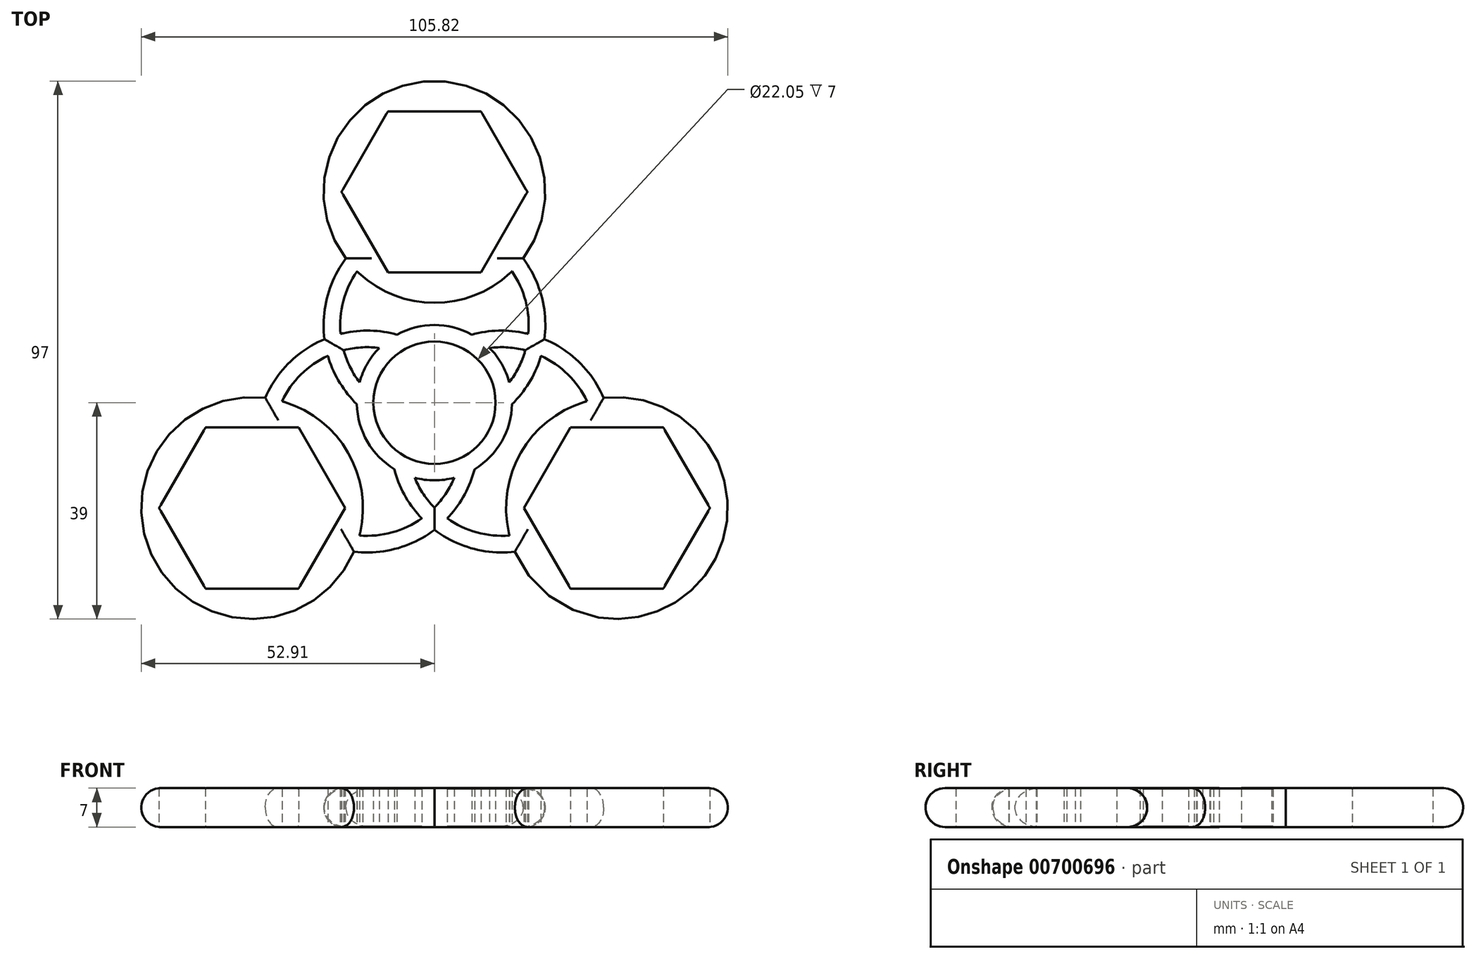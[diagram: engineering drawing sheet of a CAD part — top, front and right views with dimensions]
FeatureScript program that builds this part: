
annotation { "Feature Type Name" : "Feature", "Feature Type Description" : "" }
export const myFeature = defineFeature(function(context is Context, id is Id, definition is map)
    precondition{}
    {
        {
            var Q0;
            Q0=qCreatedBy(makeId("Top.planeOp"),FACE);
            var sketch = newSketch(context, id + "F0", { "sketchPlane" : qUnion([Q0])});
            skCircle(sketch, "E0", {"center": v(0, 0) * mm, "radius": 11.03 * mm});
            skCircle(sketch, "E1", {"center": v(0, 0) * mm, "radius": 14 * mm});
            skCircle(sketch, "E2.cCircle", {"center": v(0, 38) * mm, "radius": 14.52 * mm, "construction": true});
            skLineSegment(sketch, "E2.0", {"start": v(16.77, 38) * mm, "end": v(8.39, 23.48) * mm});
            skLineSegment(sketch, "E2.1", {"start": v(8.39, 23.47) * mm, "end": v(-8.39, 23.47) * mm});
            skLineSegment(sketch, "E2.2", {"start": v(-8.39, 23.48) * mm, "end": v(-16.77, 38) * mm});
            skLineSegment(sketch, "E2.3", {"start": v(-16.77, 38) * mm, "end": v(-8.39, 52.53) * mm});
            skLineSegment(sketch, "E2.4", {"start": v(-8.39, 52.52) * mm, "end": v(8.39, 52.52) * mm});
            skLineSegment(sketch, "E2.5", {"start": v(8.39, 52.52) * mm, "end": v(16.77, 38) * mm});
            skPoint(sketch, "E2.0.midPoint", {"position": v(12.58, 30.74) * mm});
            skCircle(sketch, "E3", {"center": v(0, 38) * mm, "radius": 20 * mm});
            skCircle(sketch, "E4", {"center": v(0, 14) * mm, "radius": 20 * mm});
            skCircle(sketch, "E5", {"center": v(0, 14) * mm, "radius": 17 * mm});
            skSolve(sketch);
        }
        {
            var Q0;
            {var subQ0=sQuery(id+"F0.wireOp",EDGE,"E2.3");Q0=makeQuery(id+"F0.imprint","IMPRINT",FACE,{"disambiguationData":[TD([[makeQuery(id+"F0.imprint","IMPRINT",EDGE,{"derivedFrom":subQ0}),1.0]])]});}
            var Q1;
            {var subQ0=sQuery(id+"F0.wireOp",EDGE,"E5");var subQ1=sQuery(id+"F0.wireOp",EDGE,"E2.1");var subQ2=makeQuery(id+"F0.imprint","INTERSECT",VERTEX,{"disambiguationData":[OD(0.0)],"derivedFrom":[subQ1,subQ0]});Q1=makeQuery(id+"F0.imprint","IMPRINT",FACE,{"disambiguationData":[TD([[makeQuery(id+"F0.imprint","IMPRINT",EDGE,{"disambiguationData":[TD([[subQ2,-1.0]])],"derivedFrom":subQ1}),1.0]])]});}
            var Q2;
            {var subQ3=sQuery(id+"F0.wireOp",EDGE,"E2.2");var subQ5=sQuery(id+"F0.wireOp",EDGE,"E2.1");var subQ6=makeQuery(id+"F0.imprint","INTERSECT",VERTEX,{"derivedFrom":[subQ5,subQ3]});Q2=makeQuery(id+"F0.imprint","IMPRINT",FACE,{"disambiguationData":[TD([[makeQuery(id+"F0.imprint","IMPRINT",EDGE,{"disambiguationData":[TD([[subQ6,1.0]])],"derivedFrom":subQ5}),1.0]])]});}
            var Q3;
            {var subQ3=sQuery(id+"F0.wireOp",EDGE,"E2.0");var subQ7=sQuery(id+"F0.wireOp",EDGE,"E2.1");var subQ8=makeQuery(id+"F0.imprint","INTERSECT",VERTEX,{"derivedFrom":[subQ3,subQ7]});Q3=makeQuery(id+"F0.imprint","IMPRINT",FACE,{"disambiguationData":[TD([[makeQuery(id+"F0.imprint","IMPRINT",EDGE,{"disambiguationData":[TD([[subQ8,1.0]])],"derivedFrom":subQ3}),1.0]])]});}
            var Q4;
            {var subQ0=sQuery(id+"F0.wireOp",EDGE,"E4");var subQ1=sQuery(id+"F0.wireOp",EDGE,"E1");var subQ2=makeQuery(id+"F0.imprint","INTERSECT",VERTEX,{"disambiguationData":[OD(1.0)],"derivedFrom":[subQ1,subQ0]});Q4=makeQuery(id+"F0.imprint","IMPRINT",FACE,{"disambiguationData":[TD([[makeQuery(id+"F0.imprint","IMPRINT",EDGE,{"disambiguationData":[TD([[subQ2,1.0]])],"derivedFrom":subQ1}),-1.0]])]});}
            var Q5;
            {var subQ0=sQuery(id+"F0.wireOp",EDGE,"E4");var subQ1=sQuery(id+"F0.wireOp",EDGE,"E1");var subQ2=makeQuery(id+"F0.imprint","INTERSECT",VERTEX,{"disambiguationData":[OD(0.0)],"derivedFrom":[subQ1,subQ0]});Q5=makeQuery(id+"F0.imprint","IMPRINT",FACE,{"disambiguationData":[TD([[makeQuery(id+"F0.imprint","IMPRINT",EDGE,{"disambiguationData":[TD([[subQ2,-1.0]])],"derivedFrom":subQ1}),-1.0]])]});}
            var Q6;
            {var subQ0=sQuery(id+"F0.wireOp",EDGE,"E5");var subQ1=sQuery(id+"F0.wireOp",EDGE,"E0");var subQ2=makeQuery(id+"F0.imprint","INTERSECT",VERTEX,{"disambiguationData":[OD(0.0)],"derivedFrom":[subQ1,subQ0]});Q6=makeQuery(id+"F0.imprint","IMPRINT",FACE,{"disambiguationData":[TD([[makeQuery(id+"F0.imprint","IMPRINT",EDGE,{"disambiguationData":[TD([[subQ2,1.0]])],"derivedFrom":subQ1}),-1.0]])]});}
            var Q7;
            {var subQ0=sQuery(id+"F0.wireOp",EDGE,"E5");var subQ1=sQuery(id+"F0.wireOp",EDGE,"E0");var subQ2=makeQuery(id+"F0.imprint","INTERSECT",VERTEX,{"disambiguationData":[OD(1.0)],"derivedFrom":[subQ1,subQ0]});Q7=makeQuery(id+"F0.imprint","IMPRINT",FACE,{"disambiguationData":[TD([[makeQuery(id+"F0.imprint","IMPRINT",EDGE,{"disambiguationData":[TD([[subQ2,-1.0]])],"derivedFrom":subQ1}),-1.0]])]});}
            var Q8;
            {var subQ0=sQuery(id+"F0.wireOp",EDGE,"E5");var subQ1=sQuery(id+"F0.wireOp",EDGE,"E0");var subQ2=makeQuery(id+"F0.imprint","INTERSECT",VERTEX,{"disambiguationData":[OD(0.0)],"derivedFrom":[subQ1,subQ0]});Q8=makeQuery(id+"F0.imprint","IMPRINT",FACE,{"disambiguationData":[TD([[makeQuery(id+"F0.imprint","IMPRINT",EDGE,{"disambiguationData":[TD([[subQ2,-1.0]])],"derivedFrom":subQ1}),-1.0]])]});}
            var Q9;
            {var subQ0=sQuery(id+"F0.wireOp",EDGE,"E4");var subQ1=sQuery(id+"F0.wireOp",EDGE,"E0");var subQ2=makeQuery(id+"F0.imprint","INTERSECT",VERTEX,{"disambiguationData":[OD(0.0)],"derivedFrom":[subQ1,subQ0]});Q9=makeQuery(id+"F0.imprint","IMPRINT",FACE,{"disambiguationData":[TD([[makeQuery(id+"F0.imprint","IMPRINT",EDGE,{"disambiguationData":[TD([[subQ2,1.0]])],"derivedFrom":subQ1}),-1.0]])]});}
            var Q10;
            {var subQ0=sQuery(id+"F0.wireOp",EDGE,"E4");var subQ1=sQuery(id+"F0.wireOp",EDGE,"E1");var subQ2=makeQuery(id+"F0.imprint","INTERSECT",VERTEX,{"disambiguationData":[OD(0.0)],"derivedFrom":[subQ1,subQ0]});Q10=makeQuery(id+"F0.imprint","IMPRINT",FACE,{"disambiguationData":[TD([[makeQuery(id+"F0.imprint","IMPRINT",EDGE,{"disambiguationData":[TD([[subQ2,1.0]])],"derivedFrom":subQ1}),-1.0]])]});}
            var Q11;
            {var subQ0=sQuery(id+"F0.wireOp",EDGE,"E4");var subQ1=sQuery(id+"F0.wireOp",EDGE,"E0");var subQ2=makeQuery(id+"F0.imprint","INTERSECT",VERTEX,{"disambiguationData":[OD(0.0)],"derivedFrom":[subQ1,subQ0]});Q11=makeQuery(id+"F0.imprint","IMPRINT",FACE,{"disambiguationData":[TD([[makeQuery(id+"F0.imprint","IMPRINT",EDGE,{"disambiguationData":[TD([[subQ2,-1.0]])],"derivedFrom":subQ1}),-1.0]])]});}
            var Q12;
            {var subQ0=sQuery(id+"F0.wireOp",EDGE,"E5");var subQ1=sQuery(id+"F0.wireOp",EDGE,"E0");var subQ2=makeQuery(id+"F0.imprint","INTERSECT",VERTEX,{"disambiguationData":[OD(1.0)],"derivedFrom":[subQ1,subQ0]});Q12=makeQuery(id+"F0.imprint","IMPRINT",FACE,{"disambiguationData":[TD([[makeQuery(id+"F0.imprint","IMPRINT",EDGE,{"disambiguationData":[TD([[subQ2,1.0]])],"derivedFrom":subQ1}),-1.0]])]});}
            var Q13;
            {var subQ0=sQuery(id+"F0.wireOp",EDGE,"E4");var subQ1=sQuery(id+"F0.wireOp",EDGE,"E1");var subQ2=makeQuery(id+"F0.imprint","INTERSECT",VERTEX,{"disambiguationData":[OD(1.0)],"derivedFrom":[subQ1,subQ0]});Q13=makeQuery(id+"F0.imprint","IMPRINT",FACE,{"disambiguationData":[TD([[makeQuery(id+"F0.imprint","IMPRINT",EDGE,{"disambiguationData":[TD([[subQ2,-1.0]])],"derivedFrom":subQ1}),-1.0]])]});}
            var Q14;
            {var subQ0=sQuery(id+"F0.wireOp",EDGE,"E4");var subQ1=sQuery(id+"F0.wireOp",EDGE,"E2.0");var subQ2=makeQuery(id+"F0.imprint","INTERSECT",VERTEX,{"derivedFrom":[subQ1,subQ0]});Q14=makeQuery(id+"F0.imprint","IMPRINT",FACE,{"disambiguationData":[TD([[makeQuery(id+"F0.imprint","IMPRINT",EDGE,{"disambiguationData":[TD([[subQ2,-1.0]])],"derivedFrom":subQ1}),1.0]])]});}
            var Q15;
            {var subQ0=sQuery(id+"F0.wireOp",EDGE,"E5");var subQ1=sQuery(id+"F0.wireOp",EDGE,"E2.2");var subQ2=makeQuery(id+"F0.imprint","INTERSECT",VERTEX,{"derivedFrom":[subQ1,subQ0]});Q15=makeQuery(id+"F0.imprint","IMPRINT",FACE,{"disambiguationData":[TD([[makeQuery(id+"F0.imprint","IMPRINT",EDGE,{"disambiguationData":[TD([[subQ2,-1.0]])],"derivedFrom":subQ1}),1.0]])]});}
            extrude(context, id + "F1", {"entities" : qUnion([Q0, Q1, Q2, Q3, Q4, Q5, Q6, Q7, Q8, Q9, Q10, Q11, Q12, Q13, Q14, Q15]), "depth" : 7 * mm, "offsetDistance" : 25 * mm});
        }
        {
            var Q0;
            Q0=makeQuery(id+"F1.opExtrude","SWEPT_BODY",BODY,{"disambiguationData":[OSD([sQuery(id+"F0.wireOp",EDGE,"E0"),sQuery(id+"F0.wireOp",EDGE,"E1"),sQuery(id+"F0.wireOp",EDGE,"E2.0"),sQuery(id+"F0.wireOp",EDGE,"E2.1"),sQuery(id+"F0.wireOp",EDGE,"E2.2"),sQuery(id+"F0.wireOp",EDGE,"E2.3"),sQuery(id+"F0.wireOp",EDGE,"E2.4"),sQuery(id+"F0.wireOp",EDGE,"E2.5"),sQuery(id+"F0.wireOp",EDGE,"E3"),sQuery(id+"F0.wireOp",EDGE,"E4"),sQuery(id+"F0.wireOp",EDGE,"E5")])]});
            var Q1;
            {var subQ0=sQuery(id+"F0.wireOp",EDGE,"E4");var subQ1=sQuery(id+"F0.wireOp",EDGE,"E1");Q1=makeQuery(id+"F1.opExtrude","SWEPT_FACE",FACE,{"disambiguationData":[OSD([subQ1]),TDD([makeQuery(id+"F0.imprint","IMPRINT",EDGE,{"disambiguationData":[TD([[makeQuery(id+"F0.imprint","INTERSECT",VERTEX,{"disambiguationData":[OD(0.0)],"derivedFrom":[subQ1,subQ0]}),-1.0]])],"derivedFrom":subQ1})])]});}
            circularPattern(context, id + "F2", {"operationType" : NewBodyOperationType.ADD, "entities" : qUnion([Q0]), "axis" : qUnion([Q1]), "angle" : 360 * degree, "instanceCount" : 3, "equalSpace" : true});
        }
        {
            var Q0;
            {var subQ0=sQuery(id+"F0.wireOp",EDGE,"E4");var subQ1=sQuery(id+"F0.wireOp",EDGE,"E3");Q0=makeQuery(id+"F1.opExtrude","CAP_EDGE",EDGE,{"disambiguationData":[OSD([subQ1]),TDD([makeQuery(id+"F0.imprint","IMPRINT",EDGE,{"disambiguationData":[TD([[makeQuery(id+"F0.imprint","INTERSECT",VERTEX,{"disambiguationData":[OD(0.0)],"derivedFrom":[subQ1,subQ0]}),1.0]])],"derivedFrom":subQ1})])],"isStart":false});}
            var Q1;
            {var subQ0=sQuery(id+"F0.wireOp",EDGE,"E4");var subQ1=sQuery(id+"F0.wireOp",EDGE,"E3");Q1=makeQuery(id+"F1.opExtrude","CAP_EDGE",EDGE,{"disambiguationData":[OSD([subQ1]),TDD([makeQuery(id+"F0.imprint","IMPRINT",EDGE,{"disambiguationData":[TD([[makeQuery(id+"F0.imprint","INTERSECT",VERTEX,{"disambiguationData":[OD(0.0)],"derivedFrom":[subQ1,subQ0]}),1.0]])],"derivedFrom":subQ1})])],"isStart":true});}
            var Q2;
            {var subQ0=sQuery(id+"F0.wireOp",EDGE,"E4");var subQ1=sQuery(id+"F0.wireOp",EDGE,"E3");Q2=makeQuery(id+"F2.opPattern","COPY",EDGE,{"derivedFrom":makeQuery(id+"F1.opExtrude","CAP_EDGE",EDGE,{"disambiguationData":[OSD([subQ1]),TDD([makeQuery(id+"F0.imprint","IMPRINT",EDGE,{"disambiguationData":[TD([[makeQuery(id+"F0.imprint","INTERSECT",VERTEX,{"disambiguationData":[OD(0.0)],"derivedFrom":[subQ1,subQ0]}),1.0]])],"derivedFrom":subQ1})])],"isStart":false}),"instanceName":"2"});}
            var Q3;
            {var subQ0=sQuery(id+"F0.wireOp",EDGE,"E4");var subQ1=sQuery(id+"F0.wireOp",EDGE,"E3");Q3=makeQuery(id+"F2.opPattern","COPY",EDGE,{"derivedFrom":makeQuery(id+"F1.opExtrude","CAP_EDGE",EDGE,{"disambiguationData":[OSD([subQ1]),TDD([makeQuery(id+"F0.imprint","IMPRINT",EDGE,{"disambiguationData":[TD([[makeQuery(id+"F0.imprint","INTERSECT",VERTEX,{"disambiguationData":[OD(0.0)],"derivedFrom":[subQ1,subQ0]}),1.0]])],"derivedFrom":subQ1})])],"isStart":true}),"instanceName":"2"});}
            var Q4;
            {var subQ0=sQuery(id+"F0.wireOp",EDGE,"E4");var subQ1=sQuery(id+"F0.wireOp",EDGE,"E3");Q4=makeQuery(id+"F2.opPattern","COPY",EDGE,{"derivedFrom":makeQuery(id+"F1.opExtrude","CAP_EDGE",EDGE,{"disambiguationData":[OSD([subQ1]),TDD([makeQuery(id+"F0.imprint","IMPRINT",EDGE,{"disambiguationData":[TD([[makeQuery(id+"F0.imprint","INTERSECT",VERTEX,{"disambiguationData":[OD(0.0)],"derivedFrom":[subQ1,subQ0]}),1.0]])],"derivedFrom":subQ1})])],"isStart":true}),"instanceName":"1"});}
            var Q5;
            {var subQ0=sQuery(id+"F0.wireOp",EDGE,"E4");var subQ1=sQuery(id+"F0.wireOp",EDGE,"E3");Q5=makeQuery(id+"F2.opPattern","COPY",EDGE,{"derivedFrom":makeQuery(id+"F1.opExtrude","CAP_EDGE",EDGE,{"disambiguationData":[OSD([subQ1]),TDD([makeQuery(id+"F0.imprint","IMPRINT",EDGE,{"disambiguationData":[TD([[makeQuery(id+"F0.imprint","INTERSECT",VERTEX,{"disambiguationData":[OD(0.0)],"derivedFrom":[subQ1,subQ0]}),1.0]])],"derivedFrom":subQ1})])],"isStart":false}),"instanceName":"1"});}
            fillet(context, id + "F3", {"entities" : qUnion([Q0, Q1, Q2, Q3, Q4, Q5]), "radius" : 3.5 * mm, "tangentPropagation" : true, "allowEdgeOverflow" : false});
        }
        {
            var Q0;
            {var subQ0=sQuery(id+"F0.wireOp",EDGE,"E4");var subQ2=sQuery(id+"F0.wireOp",EDGE,"E1");var subQ5=makeQuery(id+"F0.imprint","IMPRINT",EDGE,{"disambiguationData":[TD([[makeQuery(id+"F0.imprint","INTERSECT",VERTEX,{"disambiguationData":[OD(0.0)],"derivedFrom":[subQ2,subQ0]}),1.0]])],"derivedFrom":subQ0});Q0=makeQuery(id+"F2.boolean.opBoolean","SPLIT",EDGE,{"disambiguationData":[TD([makeQuery(id+"F2.opPattern","COPY",FACE,{"derivedFrom":makeQuery(id+"F1.opExtrude","SWEPT_FACE",FACE,{"disambiguationData":[OSD([subQ0]),TDD([makeQuery(id+"F0.imprint","IMPRINT",EDGE,{"disambiguationData":[TD([[makeQuery(id+"F0.imprint","INTERSECT",VERTEX,{"disambiguationData":[OD(1.0)],"derivedFrom":[subQ2,subQ0]}),-1.0]])],"derivedFrom":subQ0})])]}),"instanceName":"1"})])],"derivedFrom":makeQuery(id+"F2.opPattern","COPY",EDGE,{"derivedFrom":makeQuery(id+"F1.opExtrude","CAP_EDGE",EDGE,{"disambiguationData":[OSD([subQ0]),TDD([subQ5])],"isStart":false}),"instanceName":"2"})});}
            var Q1;
            {var subQ0=sQuery(id+"F0.wireOp",EDGE,"E4");var subQ2=sQuery(id+"F0.wireOp",EDGE,"E1");var subQ6=makeQuery(id+"F0.imprint","IMPRINT",EDGE,{"disambiguationData":[TD([[makeQuery(id+"F0.imprint","INTERSECT",VERTEX,{"disambiguationData":[OD(0.0)],"derivedFrom":[subQ2,subQ0]}),1.0]])],"derivedFrom":subQ0});Q1=makeQuery(id+"F2.boolean.opBoolean","SPLIT",EDGE,{"disambiguationData":[TD([makeQuery(id+"F2.opPattern","COPY",FACE,{"derivedFrom":makeQuery(id+"F1.opExtrude","SWEPT_FACE",FACE,{"disambiguationData":[OSD([subQ0]),TDD([makeQuery(id+"F0.imprint","IMPRINT",EDGE,{"disambiguationData":[TD([[makeQuery(id+"F0.imprint","INTERSECT",VERTEX,{"disambiguationData":[OD(1.0)],"derivedFrom":[subQ2,subQ0]}),-1.0]])],"derivedFrom":subQ0})])]}),"instanceName":"1"})])],"derivedFrom":makeQuery(id+"F2.opPattern","COPY",EDGE,{"derivedFrom":makeQuery(id+"F1.opExtrude","CAP_EDGE",EDGE,{"disambiguationData":[OSD([subQ0]),TDD([subQ6])],"isStart":true}),"instanceName":"2"})});}
            var Q2;
            {var subQ0=sQuery(id+"F0.wireOp",EDGE,"E4");var subQ1=sQuery(id+"F0.wireOp",EDGE,"E1");var subQ2=sQuery(id+"F0.wireOp",EDGE,"E3");var subQ4=makeQuery(id+"F0.imprint","IMPRINT",EDGE,{"disambiguationData":[TD([[makeQuery(id+"F0.imprint","INTERSECT",VERTEX,{"disambiguationData":[OD(1.0)],"derivedFrom":[subQ1,subQ0]}),-1.0]])],"derivedFrom":subQ0});var subQ5=makeQuery(id+"F0.imprint","INTERSECT",VERTEX,{"disambiguationData":[OD(0.0)],"derivedFrom":[subQ2,subQ0]});Q2=makeQuery(id+"F2.boolean.opBoolean","SPLIT",EDGE,{"disambiguationData":[TD([makeQuery(id+"F2.opPattern","COPY",FACE,{"derivedFrom":makeQuery(id+"F1.opExtrude","SWEPT_FACE",FACE,{"disambiguationData":[OSD([subQ2]),TDD([makeQuery(id+"F0.imprint","IMPRINT",EDGE,{"disambiguationData":[TD([[subQ5,1.0]])],"derivedFrom":subQ2})])]}),"instanceName":"1"})])],"derivedFrom":makeQuery(id+"F2.opPattern","COPY",EDGE,{"derivedFrom":makeQuery(id+"F1.opExtrude","CAP_EDGE",EDGE,{"disambiguationData":[OSD([subQ0]),TDD([subQ4])],"isStart":false}),"instanceName":"1"})});}
            var Q3;
            {var subQ0=sQuery(id+"F0.wireOp",EDGE,"E4");var subQ1=sQuery(id+"F0.wireOp",EDGE,"E1");var subQ2=sQuery(id+"F0.wireOp",EDGE,"E3");var subQ4=makeQuery(id+"F0.imprint","IMPRINT",EDGE,{"disambiguationData":[TD([[makeQuery(id+"F0.imprint","INTERSECT",VERTEX,{"disambiguationData":[OD(1.0)],"derivedFrom":[subQ1,subQ0]}),-1.0]])],"derivedFrom":subQ0});var subQ5=makeQuery(id+"F0.imprint","INTERSECT",VERTEX,{"disambiguationData":[OD(0.0)],"derivedFrom":[subQ2,subQ0]});Q3=makeQuery(id+"F2.boolean.opBoolean","SPLIT",EDGE,{"disambiguationData":[TD([makeQuery(id+"F2.opPattern","COPY",FACE,{"derivedFrom":makeQuery(id+"F1.opExtrude","SWEPT_FACE",FACE,{"disambiguationData":[OSD([subQ2]),TDD([makeQuery(id+"F0.imprint","IMPRINT",EDGE,{"disambiguationData":[TD([[subQ5,1.0]])],"derivedFrom":subQ2})])]}),"instanceName":"1"})])],"derivedFrom":makeQuery(id+"F2.opPattern","COPY",EDGE,{"derivedFrom":makeQuery(id+"F1.opExtrude","CAP_EDGE",EDGE,{"disambiguationData":[OSD([subQ0]),TDD([subQ4])],"isStart":true}),"instanceName":"1"})});}
            var Q4;
            {var subQ0=sQuery(id+"F0.wireOp",EDGE,"E4");var subQ4=sQuery(id+"F0.wireOp",EDGE,"E1");var subQ6=makeQuery(id+"F0.imprint","IMPRINT",EDGE,{"disambiguationData":[TD([[makeQuery(id+"F0.imprint","INTERSECT",VERTEX,{"disambiguationData":[OD(0.0)],"derivedFrom":[subQ4,subQ0]}),1.0]])],"derivedFrom":subQ0});Q4=makeQuery(id+"F2.boolean.opBoolean","SPLIT",EDGE,{"disambiguationData":[TD([makeQuery(id+"F1.opExtrude","SWEPT_FACE",FACE,{"disambiguationData":[OSD([subQ0]),TDD([makeQuery(id+"F0.imprint","IMPRINT",EDGE,{"disambiguationData":[TD([[makeQuery(id+"F0.imprint","INTERSECT",VERTEX,{"disambiguationData":[OD(1.0)],"derivedFrom":[subQ4,subQ0]}),-1.0]])],"derivedFrom":subQ0})])]})])],"derivedFrom":makeQuery(id+"F2.opPattern","COPY",EDGE,{"derivedFrom":makeQuery(id+"F1.opExtrude","CAP_EDGE",EDGE,{"disambiguationData":[OSD([subQ0]),TDD([subQ6])],"isStart":false}),"instanceName":"1"})});}
            var Q5;
            {var subQ0=sQuery(id+"F0.wireOp",EDGE,"E4");var subQ4=sQuery(id+"F0.wireOp",EDGE,"E1");var subQ6=makeQuery(id+"F0.imprint","IMPRINT",EDGE,{"disambiguationData":[TD([[makeQuery(id+"F0.imprint","INTERSECT",VERTEX,{"disambiguationData":[OD(0.0)],"derivedFrom":[subQ4,subQ0]}),1.0]])],"derivedFrom":subQ0});Q5=makeQuery(id+"F2.boolean.opBoolean","SPLIT",EDGE,{"disambiguationData":[TD([makeQuery(id+"F1.opExtrude","SWEPT_FACE",FACE,{"disambiguationData":[OSD([subQ0]),TDD([makeQuery(id+"F0.imprint","IMPRINT",EDGE,{"disambiguationData":[TD([[makeQuery(id+"F0.imprint","INTERSECT",VERTEX,{"disambiguationData":[OD(1.0)],"derivedFrom":[subQ4,subQ0]}),-1.0]])],"derivedFrom":subQ0})])]})])],"derivedFrom":makeQuery(id+"F2.opPattern","COPY",EDGE,{"derivedFrom":makeQuery(id+"F1.opExtrude","CAP_EDGE",EDGE,{"disambiguationData":[OSD([subQ0]),TDD([subQ6])],"isStart":true}),"instanceName":"1"})});}
            var Q6;
            {var subQ0=sQuery(id+"F0.wireOp",EDGE,"E4");var subQ1=sQuery(id+"F0.wireOp",EDGE,"E3");var subQ2=sQuery(id+"F0.wireOp",EDGE,"E1");var subQ4=makeQuery(id+"F0.imprint","INTERSECT",VERTEX,{"disambiguationData":[OD(0.0)],"derivedFrom":[subQ1,subQ0]});var subQ6=makeQuery(id+"F0.imprint","IMPRINT",EDGE,{"disambiguationData":[TD([[makeQuery(id+"F0.imprint","INTERSECT",VERTEX,{"disambiguationData":[OD(1.0)],"derivedFrom":[subQ2,subQ0]}),-1.0]])],"derivedFrom":subQ0});Q6=makeQuery(id+"F2.boolean.opBoolean","SPLIT",EDGE,{"disambiguationData":[TD([makeQuery(id+"F1.opExtrude","SWEPT_FACE",FACE,{"disambiguationData":[OSD([subQ1]),TDD([makeQuery(id+"F0.imprint","IMPRINT",EDGE,{"disambiguationData":[TD([[subQ4,1.0]])],"derivedFrom":subQ1})])]})])],"derivedFrom":makeQuery(id+"F1.opExtrude","CAP_EDGE",EDGE,{"disambiguationData":[OSD([subQ0]),TDD([subQ6])],"isStart":false})});}
            var Q7;
            {var subQ0=sQuery(id+"F0.wireOp",EDGE,"E4");var subQ1=sQuery(id+"F0.wireOp",EDGE,"E1");var subQ2=sQuery(id+"F0.wireOp",EDGE,"E3");var subQ4=makeQuery(id+"F0.imprint","IMPRINT",EDGE,{"disambiguationData":[TD([[makeQuery(id+"F0.imprint","INTERSECT",VERTEX,{"disambiguationData":[OD(1.0)],"derivedFrom":[subQ1,subQ0]}),-1.0]])],"derivedFrom":subQ0});var subQ6=makeQuery(id+"F0.imprint","INTERSECT",VERTEX,{"disambiguationData":[OD(0.0)],"derivedFrom":[subQ2,subQ0]});Q7=makeQuery(id+"F2.boolean.opBoolean","SPLIT",EDGE,{"disambiguationData":[TD([makeQuery(id+"F1.opExtrude","SWEPT_FACE",FACE,{"disambiguationData":[OSD([subQ2]),TDD([makeQuery(id+"F0.imprint","IMPRINT",EDGE,{"disambiguationData":[TD([[subQ6,1.0]])],"derivedFrom":subQ2})])]})])],"derivedFrom":makeQuery(id+"F1.opExtrude","CAP_EDGE",EDGE,{"disambiguationData":[OSD([subQ0]),TDD([subQ4])],"isStart":true})});}
            var Q8;
            {var subQ0=sQuery(id+"F0.wireOp",EDGE,"E4");var subQ2=sQuery(id+"F0.wireOp",EDGE,"E1");var subQ6=makeQuery(id+"F0.imprint","IMPRINT",EDGE,{"disambiguationData":[TD([[makeQuery(id+"F0.imprint","INTERSECT",VERTEX,{"disambiguationData":[OD(1.0)],"derivedFrom":[subQ2,subQ0]}),-1.0]])],"derivedFrom":subQ0});Q8=makeQuery(id+"F2.boolean.opBoolean","SPLIT",EDGE,{"disambiguationData":[TD([makeQuery(id+"F1.opExtrude","SWEPT_FACE",FACE,{"disambiguationData":[OSD([subQ0]),TDD([makeQuery(id+"F0.imprint","IMPRINT",EDGE,{"disambiguationData":[TD([[makeQuery(id+"F0.imprint","INTERSECT",VERTEX,{"disambiguationData":[OD(0.0)],"derivedFrom":[subQ2,subQ0]}),1.0]])],"derivedFrom":subQ0})])]})])],"derivedFrom":makeQuery(id+"F2.opPattern","COPY",EDGE,{"derivedFrom":makeQuery(id+"F1.opExtrude","CAP_EDGE",EDGE,{"disambiguationData":[OSD([subQ0]),TDD([subQ6])],"isStart":true}),"instanceName":"2"})});}
            var Q9;
            {var subQ0=sQuery(id+"F0.wireOp",EDGE,"E4");var subQ2=sQuery(id+"F0.wireOp",EDGE,"E1");var subQ6=makeQuery(id+"F0.imprint","IMPRINT",EDGE,{"disambiguationData":[TD([[makeQuery(id+"F0.imprint","INTERSECT",VERTEX,{"disambiguationData":[OD(1.0)],"derivedFrom":[subQ2,subQ0]}),-1.0]])],"derivedFrom":subQ0});Q9=makeQuery(id+"F2.boolean.opBoolean","SPLIT",EDGE,{"disambiguationData":[TD([makeQuery(id+"F1.opExtrude","SWEPT_FACE",FACE,{"disambiguationData":[OSD([subQ0]),TDD([makeQuery(id+"F0.imprint","IMPRINT",EDGE,{"disambiguationData":[TD([[makeQuery(id+"F0.imprint","INTERSECT",VERTEX,{"disambiguationData":[OD(0.0)],"derivedFrom":[subQ2,subQ0]}),1.0]])],"derivedFrom":subQ0})])]})])],"derivedFrom":makeQuery(id+"F2.opPattern","COPY",EDGE,{"derivedFrom":makeQuery(id+"F1.opExtrude","CAP_EDGE",EDGE,{"disambiguationData":[OSD([subQ0]),TDD([subQ6])],"isStart":false}),"instanceName":"2"})});}
            var Q10;
            {var subQ0=sQuery(id+"F0.wireOp",EDGE,"E4");var subQ1=sQuery(id+"F0.wireOp",EDGE,"E1");var subQ2=sQuery(id+"F0.wireOp",EDGE,"E3");var subQ3=makeQuery(id+"F0.imprint","INTERSECT",VERTEX,{"disambiguationData":[OD(0.0)],"derivedFrom":[subQ2,subQ0]});var subQ4=makeQuery(id+"F0.imprint","IMPRINT",EDGE,{"disambiguationData":[TD([[makeQuery(id+"F0.imprint","INTERSECT",VERTEX,{"disambiguationData":[OD(0.0)],"derivedFrom":[subQ1,subQ0]}),1.0]])],"derivedFrom":subQ0});Q10=makeQuery(id+"F2.boolean.opBoolean","SPLIT",EDGE,{"disambiguationData":[TD([makeQuery(id+"F1.opExtrude","SWEPT_FACE",FACE,{"disambiguationData":[OSD([subQ2]),TDD([makeQuery(id+"F0.imprint","IMPRINT",EDGE,{"disambiguationData":[TD([[subQ3,1.0]])],"derivedFrom":subQ2})])]})])],"derivedFrom":makeQuery(id+"F1.opExtrude","CAP_EDGE",EDGE,{"disambiguationData":[OSD([subQ0]),TDD([subQ4])],"isStart":true})});}
            var Q11;
            {var subQ0=sQuery(id+"F0.wireOp",EDGE,"E4");var subQ1=sQuery(id+"F0.wireOp",EDGE,"E3");var subQ2=sQuery(id+"F0.wireOp",EDGE,"E1");var subQ4=makeQuery(id+"F0.imprint","INTERSECT",VERTEX,{"disambiguationData":[OD(0.0)],"derivedFrom":[subQ1,subQ0]});var subQ5=makeQuery(id+"F0.imprint","IMPRINT",EDGE,{"disambiguationData":[TD([[makeQuery(id+"F0.imprint","INTERSECT",VERTEX,{"disambiguationData":[OD(0.0)],"derivedFrom":[subQ2,subQ0]}),1.0]])],"derivedFrom":subQ0});Q11=makeQuery(id+"F2.boolean.opBoolean","SPLIT",EDGE,{"disambiguationData":[TD([makeQuery(id+"F1.opExtrude","SWEPT_FACE",FACE,{"disambiguationData":[OSD([subQ1]),TDD([makeQuery(id+"F0.imprint","IMPRINT",EDGE,{"disambiguationData":[TD([[subQ4,1.0]])],"derivedFrom":subQ1})])]})])],"derivedFrom":makeQuery(id+"F1.opExtrude","CAP_EDGE",EDGE,{"disambiguationData":[OSD([subQ0]),TDD([subQ5])],"isStart":false})});}
            fillet(context, id + "F4", {"entities" : qUnion([Q0, Q1, Q2, Q3, Q4, Q5, Q6, Q7, Q8, Q9, Q10, Q11]), "radius" : 3.5 * mm, "tangentPropagation" : true, "allowEdgeOverflow" : false});
        }
    });
